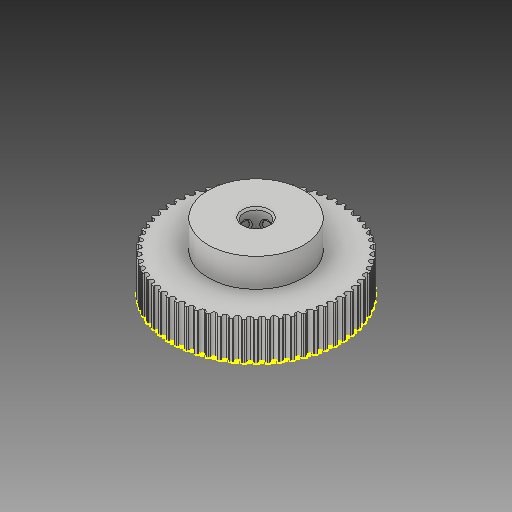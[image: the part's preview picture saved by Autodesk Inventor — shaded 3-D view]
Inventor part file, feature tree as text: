
AUTODESK INVENTOR PART (.ipt)
format: ipt  version: 2019.2 (Build 232265000, 265)  size: 1,133,056 bytes
history: native  units: mm
features: move_body x2, other x1, sketch x1, imported_body x1
ambient origin geometry x8: Origin, YZ Plane, XZ Plane, XY Plane, X Axis, Y Axis, Z Axis, Center Point
bodies: Solid1 (feature_tree)
feature tree (5):
  other  "gates_P60-3M-09AL.stp"
  move_body  "Move Body1"
  move_body  "Move Body2"
  sketch  "Sketch2"  dims[d0=90.0deg d1=90.0deg]
  imported_body  "Base1"
